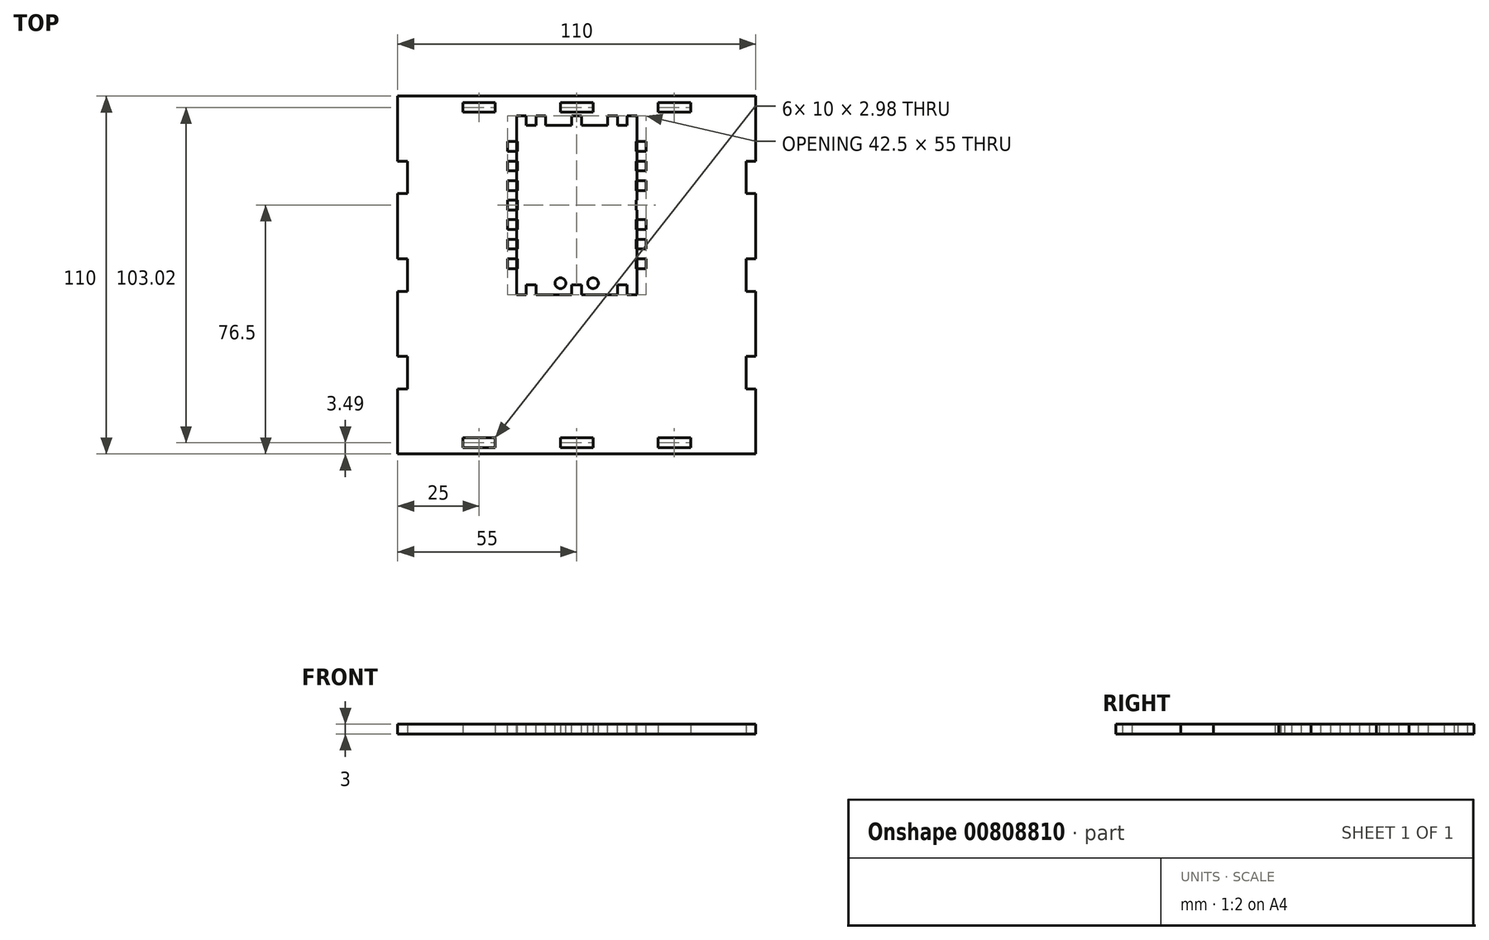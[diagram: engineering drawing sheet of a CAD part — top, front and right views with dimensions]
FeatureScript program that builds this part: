
annotation { "Feature Type Name" : "Feature", "Feature Type Description" : "" }
export const myFeature = defineFeature(function(context is Context, id is Id, definition is map)
    precondition{}
    {
        {
            var Q0;
            Q0=qCreatedBy(makeId("Top.planeOp"),FACE);
            var sketch = newSketch(context, id + "F0", { "sketchPlane" : qUnion([Q0])});
            skLineSegment(sketch, "E0.bottom", {"start": v(56, 56) * mm, "end": v(-56, 56) * mm});
            skLineSegment(sketch, "E0.top", {"start": v(56, -56) * mm, "end": v(-56, -56) * mm});
            skLineSegment(sketch, "E0.left", {"start": v(56, 56) * mm, "end": v(56, -56) * mm});
            skLineSegment(sketch, "E0.right", {"start": v(-56, 56) * mm, "end": v(-56, -56) * mm});
            skLineSegment(sketch, "E1.bottom", {"start": v(5, 50.01) * mm, "end": v(-5, 50.01) * mm});
            skLineSegment(sketch, "E1.top", {"start": v(5, 52.99) * mm, "end": v(-5, 52.99) * mm});
            skLineSegment(sketch, "E1.left", {"start": v(5, 50.01) * mm, "end": v(5, 52.99) * mm});
            skLineSegment(sketch, "E1.right", {"start": v(-5, 50) * mm, "end": v(-5, 52.99) * mm});
            skPoint(sketch, "E1.middle", {"position": v(0, 51.5) * mm});
            skLineSegment(sketch, "E2.bottom", {"start": v(-35, 50.01) * mm, "end": v(-25, 50.01) * mm});
            skLineSegment(sketch, "E2.top", {"start": v(-35, 53) * mm, "end": v(-25, 53) * mm});
            skLineSegment(sketch, "E2.left", {"start": v(-35, 50.01) * mm, "end": v(-35, 52.99) * mm});
            skLineSegment(sketch, "E2.right", {"start": v(-25, 50.01) * mm, "end": v(-25, 52.99) * mm});
            skPoint(sketch, "E2.middle", {"position": v(-30, 51.5) * mm});
            skLineSegment(sketch, "E3.bottom", {"start": v(35, 50.01) * mm, "end": v(25, 50.01) * mm});
            skLineSegment(sketch, "E3.top", {"start": v(35, 52.99) * mm, "end": v(25, 52.99) * mm});
            skLineSegment(sketch, "E3.left", {"start": v(35, 50) * mm, "end": v(35, 52.99) * mm});
            skLineSegment(sketch, "E3.right", {"start": v(25, 50) * mm, "end": v(25, 52.99) * mm});
            skPoint(sketch, "E3.middle", {"position": v(30, 51.5) * mm});
            skPoint(sketch, "E3.cornerSnap0", {"position": v(0, 50.01) * mm});
            skLineSegment(sketch, "E4.2.0", {"start": v(35, -53) * mm, "end": v(25, -53) * mm});
            skLineSegment(sketch, "E4.2.1", {"start": v(35, -50.03) * mm, "end": v(25, -50.03) * mm});
            skPoint(sketch, "E4.2.2", {"position": v(-30, -51.5) * mm});
            skLineSegment(sketch, "E4.2.3", {"start": v(-5, -53) * mm, "end": v(5, -53) * mm});
            skLineSegment(sketch, "E4.2.4", {"start": v(-35, -50.03) * mm, "end": v(-25, -50.03) * mm});
            skPoint(sketch, "E4.2.5", {"position": v(0, -50.01) * mm});
            skPoint(sketch, "E4.2.6", {"position": v(0, -51.5) * mm});
            skPoint(sketch, "E4.2.7", {"position": v(30, -51.5) * mm});
            skLineSegment(sketch, "E4.2.8", {"start": v(-5, -50.03) * mm, "end": v(5, -50.03) * mm});
            skLineSegment(sketch, "E4.2.9", {"start": v(-35, -53) * mm, "end": v(-25, -53) * mm});
            skLineSegment(sketch, "E4.2.10", {"start": v(35, -50.03) * mm, "end": v(35, -53) * mm});
            skLineSegment(sketch, "E4.2.11", {"start": v(-35, -50.03) * mm, "end": v(-35, -53) * mm});
            skLineSegment(sketch, "E4.2.12", {"start": v(-5, -50.03) * mm, "end": v(-5, -53) * mm});
            skLineSegment(sketch, "E4.2.13", {"start": v(-25, -50.03) * mm, "end": v(-25, -53) * mm});
            skLineSegment(sketch, "E4.2.14", {"start": v(5, -50.03) * mm, "end": v(5, -53) * mm});
            skLineSegment(sketch, "E4.2.15", {"start": v(25, -50.03) * mm, "end": v(25, -53) * mm});
            skLineSegment(sketch, "E5.bottom", {"start": v(-55, -55) * mm, "end": v(55, -55) * mm});
            skLineSegment(sketch, "E5.top", {"start": v(-55, 55) * mm, "end": v(55, 55) * mm});
            skLineSegment(sketch, "E5.left", {"start": v(-55, -55.01) * mm, "end": v(-55, 55) * mm});
            skLineSegment(sketch, "E5.right", {"start": v(55, -55) * mm, "end": v(55, 55) * mm});
            skLineSegment(sketch, "E6.bottom", {"start": v(-52, 4.99) * mm, "end": v(-58, 4.99) * mm});
            skLineSegment(sketch, "E6.top", {"start": v(-52, -5.01) * mm, "end": v(-58, -5.01) * mm});
            skLineSegment(sketch, "E6.left", {"start": v(-52, 4.99) * mm, "end": v(-52, -5.01) * mm});
            skLineSegment(sketch, "E6.right", {"start": v(-58, 4.99) * mm, "end": v(-58, -5.01) * mm});
            skPoint(sketch, "E6.middle", {"position": v(-55, -0.01) * mm});
            skLineSegment(sketch, "E7.bottom", {"start": v(-52, 24.99) * mm, "end": v(-58, 24.99) * mm});
            skLineSegment(sketch, "E7.top", {"start": v(-52, 34.99) * mm, "end": v(-58, 34.99) * mm});
            skLineSegment(sketch, "E7.left", {"start": v(-52, 24.99) * mm, "end": v(-52, 34.99) * mm});
            skLineSegment(sketch, "E7.right", {"start": v(-58, 24.99) * mm, "end": v(-58, 34.99) * mm});
            skPoint(sketch, "E7.middle", {"position": v(-55, 29.99) * mm});
            skLineSegment(sketch, "E8.bottom", {"start": v(-52, -25.01) * mm, "end": v(-58, -25.01) * mm});
            skLineSegment(sketch, "E8.top", {"start": v(-52, -35.01) * mm, "end": v(-58, -35.01) * mm});
            skLineSegment(sketch, "E8.left", {"start": v(-52, -25.01) * mm, "end": v(-52, -35.01) * mm});
            skLineSegment(sketch, "E8.right", {"start": v(-58, -25.01) * mm, "end": v(-58, -35.01) * mm});
            skPoint(sketch, "E8.middle", {"position": v(-55, -30.01) * mm});
            skLineSegment(sketch, "E9", {"start": v(0, 0) * mm, "end": v(0, 13.34) * mm});
            skLineSegment(sketch, "E10.MirrorCS", {"start": v(52, -35.01) * mm, "end": v(58, -35.01) * mm});
            skLineSegment(sketch, "E11.MirrorCS", {"start": v(52, -25.01) * mm, "end": v(58, -25.01) * mm});
            skLineSegment(sketch, "E12.MirrorCS", {"start": v(52, 4.99) * mm, "end": v(58, 4.99) * mm});
            skLineSegment(sketch, "E13.MirrorCS", {"start": v(52, -5.01) * mm, "end": v(58, -5.01) * mm});
            skLineSegment(sketch, "E14.MirrorCS", {"start": v(52, 35) * mm, "end": v(58, 35) * mm});
            skLineSegment(sketch, "E15.MirrorCS", {"start": v(52, 25) * mm, "end": v(58, 25) * mm});
            skLineSegment(sketch, "E16.MirrorCS", {"start": v(58, -25.01) * mm, "end": v(58, -35.01) * mm});
            skPoint(sketch, "E17.MirrorP", {"position": v(55, -30.01) * mm});
            skLineSegment(sketch, "E18.MirrorCS", {"start": v(52, 24.99) * mm, "end": v(52, 34.99) * mm});
            skPoint(sketch, "E19.MirrorP", {"position": v(55, -0.01) * mm});
            skLineSegment(sketch, "E20.MirrorCS", {"start": v(58, 4.99) * mm, "end": v(58, -5.01) * mm});
            skLineSegment(sketch, "E21.MirrorCS", {"start": v(52, -25.01) * mm, "end": v(52, -35.01) * mm});
            skPoint(sketch, "E22.MirrorP", {"position": v(55, 29.99) * mm});
            skLineSegment(sketch, "E23.MirrorCS", {"start": v(58, 24.99) * mm, "end": v(58, 34.99) * mm});
            skLineSegment(sketch, "E24.MirrorCS", {"start": v(52, 4.99) * mm, "end": v(52, -5.01) * mm});
            skSolve(sketch);
        }
        {
            var Q0;
            Q0=makeQuery(id+"F0.imprint","IMPRINT",FACE,{"disambiguationData":[TD([[makeQuery(id+"F0.imprint","IMPRINT",EDGE,{"derivedFrom":sQuery(id+"F0.wireOp",EDGE,"E1.bottom")}),1.0]])]});
            extrude(context, id + "F1", {"entities" : qUnion([Q0]), "depth" : 3 * mm, "offsetDistance" : 25 * mm});
        }
        {
            var Q0;
            Q0=makeQuery(id+"F1.opExtrude","CAP_FACE",FACE,{"disambiguationData":[OSD([sQuery(id+"F0.wireOp",EDGE,"E1.bottom"),sQuery(id+"F0.wireOp",EDGE,"E1.top"),sQuery(id+"F0.wireOp",EDGE,"E1.left"),sQuery(id+"F0.wireOp",EDGE,"E1.right"),sQuery(id+"F0.wireOp",EDGE,"E2.bottom"),sQuery(id+"F0.wireOp",EDGE,"E2.top"),sQuery(id+"F0.wireOp",EDGE,"E2.left"),sQuery(id+"F0.wireOp",EDGE,"E2.right"),sQuery(id+"F0.wireOp",EDGE,"E3.bottom"),sQuery(id+"F0.wireOp",EDGE,"E3.top"),sQuery(id+"F0.wireOp",EDGE,"E3.left"),sQuery(id+"F0.wireOp",EDGE,"E3.right"),sQuery(id+"F0.wireOp",EDGE,"E4.2.0"),sQuery(id+"F0.wireOp",EDGE,"E4.2.1"),sQuery(id+"F0.wireOp",EDGE,"E4.2.3"),sQuery(id+"F0.wireOp",EDGE,"E4.2.4"),sQuery(id+"F0.wireOp",EDGE,"E4.2.8"),sQuery(id+"F0.wireOp",EDGE,"E4.2.9"),sQuery(id+"F0.wireOp",EDGE,"E4.2.10"),sQuery(id+"F0.wireOp",EDGE,"E4.2.11"),sQuery(id+"F0.wireOp",EDGE,"E4.2.12"),sQuery(id+"F0.wireOp",EDGE,"E4.2.13"),sQuery(id+"F0.wireOp",EDGE,"E4.2.14"),sQuery(id+"F0.wireOp",EDGE,"E4.2.15"),sQuery(id+"F0.wireOp",EDGE,"0zcDC3ib-bcg3-5sZ6-BDiP-zJexwXc4272b.bottom"),sQuery(id+"F0.wireOp",EDGE,"0zcDC3ib-bcg3-5sZ6-BDiP-zJexwXc4272b.top"),sQuery(id+"F0.wireOp",EDGE,"0zcDC3ib-bcg3-5sZ6-BDiP-zJexwXc4272b.left"),sQuery(id+"F0.wireOp",EDGE,"0zcDC3ib-bcg3-5sZ6-BDiP-zJexwXc4272b.right"),sQuery(id+"F0.wireOp",EDGE,"AYckzOQu-6AoG-rlAT-OC1d-WLOSyRdi4t6B.bottom"),sQuery(id+"F0.wireOp",EDGE,"AYckzOQu-6AoG-rlAT-OC1d-WLOSyRdi4t6B.top"),sQuery(id+"F0.wireOp",EDGE,"AYckzOQu-6AoG-rlAT-OC1d-WLOSyRdi4t6B.left"),sQuery(id+"F0.wireOp",EDGE,"AYckzOQu-6AoG-rlAT-OC1d-WLOSyRdi4t6B.right"),sQuery(id+"F0.wireOp",EDGE,"v7SjSU9A-ZMWt-pp7a-Yyk7-2Wle3bSg0qv4.bottom"),sQuery(id+"F0.wireOp",EDGE,"v7SjSU9A-ZMWt-pp7a-Yyk7-2Wle3bSg0qv4.top"),sQuery(id+"F0.wireOp",EDGE,"v7SjSU9A-ZMWt-pp7a-Yyk7-2Wle3bSg0qv4.left"),sQuery(id+"F0.wireOp",EDGE,"v7SjSU9A-ZMWt-pp7a-Yyk7-2Wle3bSg0qv4.right"),sQuery(id+"F0.wireOp",EDGE,"be98ada6-46cd-47df-a602-7366731bf80c0.MirrorCS"),sQuery(id+"F0.wireOp",EDGE,"be98ada6-46cd-47df-a602-7366731bf80c1.MirrorCS"),sQuery(id+"F0.wireOp",EDGE,"be98ada6-46cd-47df-a602-7366731bf80c2.MirrorCS"),sQuery(id+"F0.wireOp",EDGE,"be98ada6-46cd-47df-a602-7366731bf80c3.MirrorCS"),sQuery(id+"F0.wireOp",EDGE,"be98ada6-46cd-47df-a602-7366731bf80c4.MirrorCS"),sQuery(id+"F0.wireOp",EDGE,"be98ada6-46cd-47df-a602-7366731bf80c5.MirrorCS"),sQuery(id+"F0.wireOp",EDGE,"be98ada6-46cd-47df-a602-7366731bf80c6.MirrorCS"),sQuery(id+"F0.wireOp",EDGE,"be98ada6-46cd-47df-a602-7366731bf80c7.MirrorCS"),sQuery(id+"F0.wireOp",EDGE,"be98ada6-46cd-47df-a602-7366731bf80c8.MirrorCS"),sQuery(id+"F0.wireOp",EDGE,"be98ada6-46cd-47df-a602-7366731bf80c10.MirrorCS"),sQuery(id+"F0.wireOp",EDGE,"be98ada6-46cd-47df-a602-7366731bf80c11.MirrorCS"),sQuery(id+"F0.wireOp",EDGE,"be98ada6-46cd-47df-a602-7366731bf80c12.MirrorCS"),sQuery(id+"F0.wireOp",EDGE,"E5.bottom"),sQuery(id+"F0.wireOp",EDGE,"E5.top"),sQuery(id+"F0.wireOp",EDGE,"E5.left"),sQuery(id+"F0.wireOp",EDGE,"E5.right")])],"isStart":false});
            var sketch = newSketch(context, id + "F2", { "sketchPlane" : qUnion([Q0])});
            skLineSegment(sketch, "E25.bottom", {"start": v(21.25, -6) * mm, "end": v(-21.25, -6) * mm});
            skLineSegment(sketch, "E25.top", {"start": v(21.25, 49) * mm, "end": v(-21.25, 49) * mm});
            skLineSegment(sketch, "E25.left", {"start": v(21.25, -6) * mm, "end": v(21.25, 49) * mm});
            skLineSegment(sketch, "E25.right", {"start": v(-21.25, -6.01) * mm, "end": v(-21.25, 49) * mm});
            skPoint(sketch, "E25.middle", {"position": v(0, 21.5) * mm});
            skLineSegment(sketch, "E26.bottom", {"start": v(-18.25, 19.99) * mm, "end": v(-24.25, 19.99) * mm});
            skLineSegment(sketch, "E26.top", {"start": v(-18.25, 22.99) * mm, "end": v(-24.25, 22.99) * mm});
            skLineSegment(sketch, "E26.left", {"start": v(-18.25, 19.99) * mm, "end": v(-18.25, 22.99) * mm});
            skLineSegment(sketch, "E26.right", {"start": v(-24.25, 19.99) * mm, "end": v(-24.25, 22.99) * mm});
            skPoint(sketch, "E26.middle", {"position": v(-21.25, 21.49) * mm});
            skLineSegment(sketch, "E27.bottom", {"start": v(24.25, 20) * mm, "end": v(18.25, 20) * mm});
            skLineSegment(sketch, "E27.top", {"start": v(24.25, 23) * mm, "end": v(18.25, 23) * mm});
            skLineSegment(sketch, "E27.left", {"start": v(24.25, 20) * mm, "end": v(24.25, 23) * mm});
            skLineSegment(sketch, "E27.right", {"start": v(18.25, 20) * mm, "end": v(18.25, 23) * mm});
            skPoint(sketch, "E27.middle", {"position": v(21.25, 21.5) * mm});
            skLineSegment(sketch, "E28.bottom", {"start": v(1.5, -9) * mm, "end": v(-1.5, -9) * mm});
            skLineSegment(sketch, "E28.top", {"start": v(1.5, -3) * mm, "end": v(-1.5, -3) * mm});
            skLineSegment(sketch, "E28.left", {"start": v(1.5, -9) * mm, "end": v(1.5, -3) * mm});
            skLineSegment(sketch, "E28.right", {"start": v(-1.5, -9) * mm, "end": v(-1.5, -3) * mm});
            skPoint(sketch, "E28.middle", {"position": v(0, -6) * mm});
            skLineSegment(sketch, "E29.bottom", {"start": v(1.5, 45.99) * mm, "end": v(-1.5, 45.99) * mm});
            skLineSegment(sketch, "E29.top", {"start": v(1.5, 52) * mm, "end": v(-1.5, 52) * mm});
            skLineSegment(sketch, "E29.left", {"start": v(1.5, 46) * mm, "end": v(1.5, 52) * mm});
            skLineSegment(sketch, "E29.right", {"start": v(-1.5, 46) * mm, "end": v(-1.5, 52) * mm});
            skPoint(sketch, "E29.middle", {"position": v(0, 49) * mm});
            skLineSegment(sketch, "E30.bottom", {"start": v(-9.7, 1.54) * mm, "end": v(9.7, 1.54) * mm});
            skLineSegment(sketch, "E30.top", {"start": v(-9.7, 41.44) * mm, "end": v(9.7, 41.44) * mm});
            skLineSegment(sketch, "E30.left", {"start": v(-9.7, 1.54) * mm, "end": v(-9.7, 41.44) * mm});
            skLineSegment(sketch, "E30.right", {"start": v(9.7, 1.54) * mm, "end": v(9.7, 41.44) * mm});
            skLineSegment(sketch, "E31.bottom", {"start": v(-18.25, 13.99) * mm, "end": v(-24.25, 13.99) * mm});
            skLineSegment(sketch, "E31.top", {"start": v(-18.25, 16.99) * mm, "end": v(-24.25, 16.99) * mm});
            skLineSegment(sketch, "E31.left", {"start": v(-18.25, 13.99) * mm, "end": v(-18.25, 16.99) * mm});
            skLineSegment(sketch, "E31.right", {"start": v(-24.25, 13.99) * mm, "end": v(-24.25, 16.99) * mm});
            skPoint(sketch, "E31.middle", {"position": v(-21.25, 15.5) * mm});
            skLineSegment(sketch, "E32.bottom", {"start": v(-18.25, 25.99) * mm, "end": v(-24.25, 25.99) * mm});
            skLineSegment(sketch, "E32.top", {"start": v(-18.25, 28.99) * mm, "end": v(-24.25, 28.99) * mm});
            skLineSegment(sketch, "E32.left", {"start": v(-18.25, 25.99) * mm, "end": v(-18.25, 28.99) * mm});
            skLineSegment(sketch, "E32.right", {"start": v(-24.25, 25.99) * mm, "end": v(-24.25, 28.99) * mm});
            skPoint(sketch, "E32.middle", {"position": v(-21.25, 27.49) * mm});
            skLineSegment(sketch, "E33.bottom", {"start": v(-18.25, 31.99) * mm, "end": v(-24.25, 31.99) * mm});
            skLineSegment(sketch, "E33.top", {"start": v(-18.25, 34.99) * mm, "end": v(-24.25, 34.99) * mm});
            skLineSegment(sketch, "E33.left", {"start": v(-18.25, 31.99) * mm, "end": v(-18.25, 34.99) * mm});
            skLineSegment(sketch, "E33.right", {"start": v(-24.25, 31.99) * mm, "end": v(-24.25, 35) * mm});
            skPoint(sketch, "E33.middle", {"position": v(-21.25, 33.49) * mm});
            skLineSegment(sketch, "E34.bottom", {"start": v(-18.25, 8) * mm, "end": v(-24.25, 8) * mm});
            skLineSegment(sketch, "E34.top", {"start": v(-18.25, 11) * mm, "end": v(-24.25, 11) * mm});
            skLineSegment(sketch, "E34.left", {"start": v(-18.25, 8) * mm, "end": v(-18.25, 11) * mm});
            skLineSegment(sketch, "E34.right", {"start": v(-24.25, 8) * mm, "end": v(-24.25, 11) * mm});
            skPoint(sketch, "E34.middle", {"position": v(-21.25, 9.5) * mm});
            skLineSegment(sketch, "E35.bottom", {"start": v(-18.25, 37.99) * mm, "end": v(-24.25, 37.99) * mm});
            skLineSegment(sketch, "E35.top", {"start": v(-18.25, 41) * mm, "end": v(-24.25, 41) * mm});
            skLineSegment(sketch, "E35.left", {"start": v(-18.25, 37.99) * mm, "end": v(-18.25, 41) * mm});
            skLineSegment(sketch, "E35.right", {"start": v(-24.25, 37.99) * mm, "end": v(-24.25, 41) * mm});
            skPoint(sketch, "E35.middle", {"position": v(-21.25, 39.49) * mm});
            skLineSegment(sketch, "E36.bottom", {"start": v(-18.25, 2) * mm, "end": v(-24.25, 1.99) * mm});
            skLineSegment(sketch, "E36.top", {"start": v(-18.25, 4.99) * mm, "end": v(-24.25, 4.99) * mm});
            skLineSegment(sketch, "E36.left", {"start": v(-18.25, 2) * mm, "end": v(-18.25, 4.99) * mm});
            skLineSegment(sketch, "E36.right", {"start": v(-24.25, 1.99) * mm, "end": v(-24.25, 4.99) * mm});
            skPoint(sketch, "E36.middle", {"position": v(-21.25, 3.5) * mm});
            skLineSegment(sketch, "E37", {"start": v(0, 21.5) * mm, "end": v(0, 24.95) * mm});
            skLineSegment(sketch, "E38.MirrorCS", {"start": v(24.25, 25.99) * mm, "end": v(24.25, 28.99) * mm});
            skLineSegment(sketch, "E39.MirrorCS", {"start": v(24.25, 8) * mm, "end": v(24.25, 11) * mm});
            skLineSegment(sketch, "E40.MirrorCS", {"start": v(18.25, 8) * mm, "end": v(18.25, 11) * mm});
            skLineSegment(sketch, "E41.MirrorCS", {"start": v(18.25, 31.99) * mm, "end": v(18.25, 34.99) * mm});
            skLineSegment(sketch, "E42.MirrorCS", {"start": v(18.25, 19.99) * mm, "end": v(18.25, 22.99) * mm});
            skLineSegment(sketch, "E43.MirrorCS", {"start": v(24.25, 19.99) * mm, "end": v(24.25, 22.99) * mm});
            skLineSegment(sketch, "E44.MirrorCS", {"start": v(18.25, 25.99) * mm, "end": v(18.25, 28.99) * mm});
            skLineSegment(sketch, "E45.MirrorCS", {"start": v(18.25, 37.99) * mm, "end": v(18.25, 41) * mm});
            skLineSegment(sketch, "E46.MirrorCS", {"start": v(24.25, 31.99) * mm, "end": v(24.25, 35) * mm});
            skLineSegment(sketch, "E47.MirrorCS", {"start": v(24.25, 37.99) * mm, "end": v(24.25, 41) * mm});
            skLineSegment(sketch, "E48.MirrorCS", {"start": v(18.25, 31.99) * mm, "end": v(24.25, 31.99) * mm});
            skLineSegment(sketch, "E49.MirrorCS", {"start": v(18.25, 17) * mm, "end": v(24.25, 17) * mm});
            skLineSegment(sketch, "E50.MirrorCS", {"start": v(18.25, 41) * mm, "end": v(24.25, 41) * mm});
            skLineSegment(sketch, "E51.MirrorCS", {"start": v(18.25, 20) * mm, "end": v(24.25, 20) * mm});
            skLineSegment(sketch, "E52.MirrorCS", {"start": v(18.25, 23) * mm, "end": v(24.25, 23) * mm});
            skLineSegment(sketch, "E53.MirrorCS", {"start": v(18.25, 37.99) * mm, "end": v(24.25, 37.99) * mm});
            skLineSegment(sketch, "E54.MirrorCS", {"start": v(18.25, 35) * mm, "end": v(24.25, 35) * mm});
            skLineSegment(sketch, "E55.MirrorCS", {"start": v(18.25, 11) * mm, "end": v(24.25, 11) * mm});
            skLineSegment(sketch, "E56.MirrorCS", {"start": v(18.25, 25.99) * mm, "end": v(24.25, 25.99) * mm});
            skLineSegment(sketch, "E57.MirrorCS", {"start": v(18.25, 2) * mm, "end": v(24.25, 2) * mm});
            skLineSegment(sketch, "E58.MirrorCS", {"start": v(18.25, 28.99) * mm, "end": v(24.25, 28.99) * mm});
            skLineSegment(sketch, "E59.MirrorCS", {"start": v(18.25, 8) * mm, "end": v(24.25, 8) * mm});
            skLineSegment(sketch, "E60.MirrorCS", {"start": v(24.25, 1.99) * mm, "end": v(24.25, 4.99) * mm});
            skLineSegment(sketch, "E61.MirrorCS", {"start": v(18.25, 14) * mm, "end": v(24.25, 14) * mm});
            skPoint(sketch, "E62.MirrorP", {"position": v(21.25, 15.5) * mm});
            skPoint(sketch, "E63.MirrorP", {"position": v(21.25, 27.49) * mm});
            skLineSegment(sketch, "E64.MirrorCS", {"start": v(18.25, 2) * mm, "end": v(18.25, 4.99) * mm});
            skPoint(sketch, "E65.MirrorP", {"position": v(21.25, 39.49) * mm});
            skLineSegment(sketch, "E66.MirrorCS", {"start": v(18.25, 13.99) * mm, "end": v(18.25, 16.99) * mm});
            skPoint(sketch, "E67.MirrorP", {"position": v(21.25, 33.49) * mm});
            skLineSegment(sketch, "E68.MirrorCS", {"start": v(18.25, 5) * mm, "end": v(24.25, 5) * mm});
            skPoint(sketch, "E69.MirrorP", {"position": v(21.25, 9.5) * mm});
            skLineSegment(sketch, "E70.MirrorCS", {"start": v(24.25, 13.99) * mm, "end": v(24.25, 16.99) * mm});
            skPoint(sketch, "E71.MirrorP", {"position": v(21.25, 3.5) * mm});
            skCircle(sketch, "E72", {"center": v(5, 45.5) * mm, "radius": 1.65 * mm});
            skCircle(sketch, "E73", {"center": v(-5, 45.5) * mm, "radius": 1.65 * mm});
            skCircle(sketch, "E74", {"center": v(-5, -2.5) * mm, "radius": 1.65 * mm});
            skCircle(sketch, "E75", {"center": v(5, -2.5) * mm, "radius": 1.65 * mm});
            skLineSegment(sketch, "E76.bottom", {"start": v(-12.5, 46) * mm, "end": v(-9.5, 46) * mm});
            skLineSegment(sketch, "E76.top", {"start": v(-12.5, 52) * mm, "end": v(-9.5, 52) * mm});
            skLineSegment(sketch, "E76.left", {"start": v(-12.5, 46) * mm, "end": v(-12.5, 52) * mm});
            skLineSegment(sketch, "E76.right", {"start": v(-9.5, 46) * mm, "end": v(-9.5, 52) * mm});
            skPoint(sketch, "E76.middle", {"position": v(-11, 49) * mm});
            skLineSegment(sketch, "E77.bottom", {"start": v(-15.5, 46) * mm, "end": v(-18.5, 46) * mm});
            skLineSegment(sketch, "E77.top", {"start": v(-15.5, 52) * mm, "end": v(-18.5, 52) * mm});
            skLineSegment(sketch, "E77.left", {"start": v(-15.5, 46) * mm, "end": v(-15.5, 52) * mm});
            skLineSegment(sketch, "E77.right", {"start": v(-18.5, 46) * mm, "end": v(-18.5, 52) * mm});
            skPoint(sketch, "E77.middle", {"position": v(-17, 49) * mm});
            skLineSegment(sketch, "E78.MirrorCS", {"start": v(9.5, 46) * mm, "end": v(9.5, 52) * mm});
            skLineSegment(sketch, "E79.MirrorCS", {"start": v(12.5, 52) * mm, "end": v(9.5, 52) * mm});
            skLineSegment(sketch, "E80.MirrorCS", {"start": v(12.5, 46) * mm, "end": v(12.5, 52) * mm});
            skLineSegment(sketch, "E81.MirrorCS", {"start": v(12.5, 46) * mm, "end": v(9.5, 46) * mm});
            skLineSegment(sketch, "E82.MirrorCS", {"start": v(15.5, 46) * mm, "end": v(18.5, 46) * mm});
            skLineSegment(sketch, "E83.MirrorCS", {"start": v(15.5, 46) * mm, "end": v(15.5, 52) * mm});
            skLineSegment(sketch, "E84.MirrorCS", {"start": v(15.5, 52) * mm, "end": v(18.5, 52) * mm});
            skLineSegment(sketch, "E85.MirrorCS", {"start": v(18.5, 46) * mm, "end": v(18.5, 52) * mm});
            skPoint(sketch, "E86.MirrorP", {"position": v(11, 49) * mm});
            skPoint(sketch, "E87.MirrorP", {"position": v(17, 49) * mm});
            skLineSegment(sketch, "E88", {"start": v(0, 21.5) * mm, "end": v(5.15, 21.5) * mm});
            skLineSegment(sketch, "E89.MirrorCS", {"start": v(-15.5, -9) * mm, "end": v(-18.5, -9) * mm});
            skLineSegment(sketch, "E90.MirrorCS", {"start": v(-12.5, -9) * mm, "end": v(-9.5, -9) * mm});
            skLineSegment(sketch, "E91.MirrorCS", {"start": v(-15.5, -3) * mm, "end": v(-18.5, -3) * mm});
            skLineSegment(sketch, "E92.MirrorCS", {"start": v(15.5, -3) * mm, "end": v(18.5, -3) * mm});
            skLineSegment(sketch, "E93.MirrorCS", {"start": v(12.5, -3) * mm, "end": v(9.5, -3) * mm});
            skLineSegment(sketch, "E94.MirrorCS", {"start": v(12.5, -9) * mm, "end": v(9.5, -9) * mm});
            skLineSegment(sketch, "E95.MirrorCS", {"start": v(15.5, -9) * mm, "end": v(18.5, -9) * mm});
            skLineSegment(sketch, "E96.MirrorCS", {"start": v(-12.5, -3) * mm, "end": v(-9.5, -3) * mm});
            skLineSegment(sketch, "E97.MirrorCS", {"start": v(-9.5, -3) * mm, "end": v(-9.5, -9) * mm});
            skLineSegment(sketch, "E98.MirrorCS", {"start": v(-18.5, -3) * mm, "end": v(-18.5, -9) * mm});
            skLineSegment(sketch, "E99.MirrorCS", {"start": v(9.5, -3) * mm, "end": v(9.5, -9) * mm});
            skLineSegment(sketch, "E100.MirrorCS", {"start": v(-15.5, -3) * mm, "end": v(-15.5, -9) * mm});
            skLineSegment(sketch, "E101.MirrorCS", {"start": v(12.5, -3) * mm, "end": v(12.5, -9) * mm});
            skLineSegment(sketch, "E102.MirrorCS", {"start": v(-12.5, -3) * mm, "end": v(-12.5, -9) * mm});
            skLineSegment(sketch, "E103.MirrorCS", {"start": v(21.25, 48.99) * mm, "end": v(21.25, -6) * mm});
            skLineSegment(sketch, "E104.MirrorCS", {"start": v(15.5, -3) * mm, "end": v(15.5, -9) * mm});
            skLineSegment(sketch, "E105.MirrorCS", {"start": v(18.5, -3) * mm, "end": v(18.5, -9) * mm});
            skLineSegment(sketch, "E106.MirrorCS", {"start": v(-1.5, -3) * mm, "end": v(-1.5, -9) * mm});
            skLineSegment(sketch, "E107.MirrorCS", {"start": v(1.5, -3) * mm, "end": v(1.5, -9) * mm});
            skLineSegment(sketch, "E108.MirrorCS", {"start": v(21.25, 49) * mm, "end": v(21.25, -6) * mm});
            skPoint(sketch, "E109.MirrorP", {"position": v(11, -6) * mm});
            skPoint(sketch, "E110.MirrorP", {"position": v(-17, -6) * mm});
            skPoint(sketch, "E111.MirrorP", {"position": v(-11, -6) * mm});
            skPoint(sketch, "E112.MirrorP", {"position": v(17, -6) * mm});
            skLineSegment(sketch, "E113.MirrorCS", {"start": v(-21.25, 49) * mm, "end": v(-21.25, -6) * mm});
            skLineSegment(sketch, "E114.bottom", {"start": v(-18.5, 46) * mm, "end": v(18.5, 46) * mm});
            skLineSegment(sketch, "E114.top", {"start": v(-18.5, -3) * mm, "end": v(18.5, -3) * mm});
            skLineSegment(sketch, "E114.left", {"start": v(-18.5, 46) * mm, "end": v(-18.5, -3) * mm});
            skLineSegment(sketch, "E114.right", {"start": v(18.5, 46) * mm, "end": v(18.5, -3) * mm});
            skSolve(sketch);
        }
        {
            var Q0;
            {var subQ0=sQuery(id+"F2.wireOp",EDGE,"E114.left");var subQ1=sQuery(id+"F2.wireOp",EDGE,"E35.bottom");var subQ2=makeQuery(id+"F2.imprint","INTERSECT",VERTEX,{"derivedFrom":[subQ1,subQ0]});Q0=makeQuery(id+"F2.imprint","IMPRINT",FACE,{"disambiguationData":[TD([[makeQuery(id+"F2.imprint","IMPRINT",EDGE,{"disambiguationData":[TD([[subQ2,-1.0]])],"derivedFrom":subQ1}),-1.0]])]});}
            var Q1;
            {var subQ0=sQuery(id+"F2.wireOp",EDGE,"E114.left");var subQ1=sQuery(id+"F2.wireOp",EDGE,"E33.bottom");var subQ2=makeQuery(id+"F2.imprint","INTERSECT",VERTEX,{"derivedFrom":[subQ1,subQ0]});Q1=makeQuery(id+"F2.imprint","IMPRINT",FACE,{"disambiguationData":[TD([[makeQuery(id+"F2.imprint","IMPRINT",EDGE,{"disambiguationData":[TD([[subQ2,-1.0]])],"derivedFrom":subQ1}),-1.0]])]});}
            var Q2;
            {var subQ0=sQuery(id+"F2.wireOp",EDGE,"E114.left");var subQ1=sQuery(id+"F2.wireOp",EDGE,"E32.bottom");var subQ2=makeQuery(id+"F2.imprint","INTERSECT",VERTEX,{"derivedFrom":[subQ1,subQ0]});Q2=makeQuery(id+"F2.imprint","IMPRINT",FACE,{"disambiguationData":[TD([[makeQuery(id+"F2.imprint","IMPRINT",EDGE,{"disambiguationData":[TD([[subQ2,-1.0]])],"derivedFrom":subQ1}),-1.0]])]});}
            var Q3;
            {var subQ0=sQuery(id+"F2.wireOp",EDGE,"E114.left");var subQ1=sQuery(id+"F2.wireOp",EDGE,"E26.bottom");var subQ2=makeQuery(id+"F2.imprint","INTERSECT",VERTEX,{"derivedFrom":[subQ1,subQ0]});Q3=makeQuery(id+"F2.imprint","IMPRINT",FACE,{"disambiguationData":[TD([[makeQuery(id+"F2.imprint","IMPRINT",EDGE,{"disambiguationData":[TD([[subQ2,-1.0]])],"derivedFrom":subQ1}),-1.0]])]});}
            var Q4;
            {var subQ0=sQuery(id+"F2.wireOp",EDGE,"E114.left");var subQ1=sQuery(id+"F2.wireOp",EDGE,"E31.bottom");var subQ2=makeQuery(id+"F2.imprint","INTERSECT",VERTEX,{"derivedFrom":[subQ1,subQ0]});Q4=makeQuery(id+"F2.imprint","IMPRINT",FACE,{"disambiguationData":[TD([[makeQuery(id+"F2.imprint","IMPRINT",EDGE,{"disambiguationData":[TD([[subQ2,-1.0]])],"derivedFrom":subQ1}),-1.0]])]});}
            var Q5;
            {var subQ0=sQuery(id+"F2.wireOp",EDGE,"E114.left");var subQ1=sQuery(id+"F2.wireOp",EDGE,"E34.bottom");var subQ2=makeQuery(id+"F2.imprint","INTERSECT",VERTEX,{"derivedFrom":[subQ1,subQ0]});Q5=makeQuery(id+"F2.imprint","IMPRINT",FACE,{"disambiguationData":[TD([[makeQuery(id+"F2.imprint","IMPRINT",EDGE,{"disambiguationData":[TD([[subQ2,-1.0]])],"derivedFrom":subQ1}),-1.0]])]});}
            var Q6;
            {var subQ0=sQuery(id+"F2.wireOp",EDGE,"E114.left");var subQ1=sQuery(id+"F2.wireOp",EDGE,"E36.bottom");var subQ2=makeQuery(id+"F2.imprint","INTERSECT",VERTEX,{"derivedFrom":[subQ1,subQ0]});Q6=makeQuery(id+"F2.imprint","IMPRINT",FACE,{"disambiguationData":[TD([[makeQuery(id+"F2.imprint","IMPRINT",EDGE,{"disambiguationData":[TD([[subQ2,-1.0]])],"derivedFrom":subQ1}),-1.0]])]});}
            var Q7;
            {var subQ0=sQuery(id+"F2.wireOp",EDGE,"E114.top");var subQ5=sQuery(id+"F2.wireOp",EDGE,"E100.MirrorCS");var subQ6=makeQuery(id+"F2.imprint","INTERSECT",VERTEX,{"derivedFrom":[subQ5,subQ0]});Q7=makeQuery(id+"F2.imprint","IMPRINT",FACE,{"disambiguationData":[TD([[makeQuery(id+"F2.imprint","IMPRINT",EDGE,{"disambiguationData":[TD([[subQ6,-1.0]])],"derivedFrom":subQ5}),-1.0]])]});}
            var Q8;
            {var subQ0=sQuery(id+"F2.wireOp",EDGE,"E114.top");var subQ1=sQuery(id+"F2.wireOp",EDGE,"E97.MirrorCS");var subQ2=makeQuery(id+"F2.imprint","INTERSECT",VERTEX,{"derivedFrom":[subQ1,subQ0]});Q8=makeQuery(id+"F2.imprint","IMPRINT",FACE,{"disambiguationData":[TD([[makeQuery(id+"F2.imprint","IMPRINT",EDGE,{"disambiguationData":[TD([[subQ2,-1.0]])],"derivedFrom":subQ1}),-1.0]])]});}
            var Q9;
            {var subQ0=sQuery(id+"F2.wireOp",EDGE,"E114.top");var subQ1=sQuery(id+"F2.wireOp",EDGE,"E106.MirrorCS");var subQ2=makeQuery(id+"F2.imprint","INTERSECT",VERTEX,{"derivedFrom":[subQ1,subQ0]});Q9=makeQuery(id+"F2.imprint","IMPRINT",FACE,{"disambiguationData":[TD([[makeQuery(id+"F2.imprint","IMPRINT",EDGE,{"disambiguationData":[TD([[subQ2,-1.0]])],"derivedFrom":subQ1}),1.0]])]});}
            var Q10;
            {var subQ0=sQuery(id+"F2.wireOp",EDGE,"E114.top");var subQ1=sQuery(id+"F2.wireOp",EDGE,"E99.MirrorCS");var subQ2=makeQuery(id+"F2.imprint","INTERSECT",VERTEX,{"derivedFrom":[subQ1,subQ0]});Q10=makeQuery(id+"F2.imprint","IMPRINT",FACE,{"disambiguationData":[TD([[makeQuery(id+"F2.imprint","IMPRINT",EDGE,{"disambiguationData":[TD([[subQ2,-1.0]])],"derivedFrom":subQ1}),1.0]])]});}
            var Q11;
            {var subQ0=sQuery(id+"F2.wireOp",EDGE,"E114.top");var subQ1=sQuery(id+"F2.wireOp",EDGE,"E104.MirrorCS");var subQ2=makeQuery(id+"F2.imprint","INTERSECT",VERTEX,{"derivedFrom":[subQ1,subQ0]});Q11=makeQuery(id+"F2.imprint","IMPRINT",FACE,{"disambiguationData":[TD([[makeQuery(id+"F2.imprint","IMPRINT",EDGE,{"disambiguationData":[TD([[subQ2,-1.0]])],"derivedFrom":subQ1}),1.0]])]});}
            var Q12;
            {var subQ45=sQuery(id+"F2.wireOp",EDGE,"E26.left");Q12=makeQuery(id+"F2.imprint","IMPRINT",FACE,{"disambiguationData":[TD([[makeQuery(id+"F2.imprint","IMPRINT",EDGE,{"derivedFrom":subQ45}),-1.0]])]});}
            var Q13;
            Q13=makeQuery(id+"F2.imprint","IMPRINT",FACE,{"disambiguationData":[TD([[makeQuery(id+"F2.imprint","IMPRINT",EDGE,{"derivedFrom":sQuery(id+"F2.wireOp",EDGE,"E30.bottom")}),1.0]])]});
            var Q14;
            {var subQ0=sQuery(id+"F2.wireOp",EDGE,"E114.right");var subQ1=sQuery(id+"F2.wireOp",EDGE,"E57.MirrorCS");var subQ2=makeQuery(id+"F2.imprint","INTERSECT",VERTEX,{"derivedFrom":[subQ1,subQ0]});Q14=makeQuery(id+"F2.imprint","IMPRINT",FACE,{"disambiguationData":[TD([[makeQuery(id+"F2.imprint","IMPRINT",EDGE,{"disambiguationData":[TD([[subQ2,-1.0]])],"derivedFrom":subQ1}),1.0]])]});}
            var Q15;
            {var subQ0=sQuery(id+"F2.wireOp",EDGE,"E114.right");var subQ1=sQuery(id+"F2.wireOp",EDGE,"E55.MirrorCS");var subQ2=makeQuery(id+"F2.imprint","INTERSECT",VERTEX,{"derivedFrom":[subQ1,subQ0]});Q15=makeQuery(id+"F2.imprint","IMPRINT",FACE,{"disambiguationData":[TD([[makeQuery(id+"F2.imprint","IMPRINT",EDGE,{"disambiguationData":[TD([[subQ2,-1.0]])],"derivedFrom":subQ1}),-1.0]])]});}
            var Q16;
            {var subQ0=sQuery(id+"F2.wireOp",EDGE,"E114.right");var subQ1=sQuery(id+"F2.wireOp",EDGE,"E49.MirrorCS");var subQ2=makeQuery(id+"F2.imprint","INTERSECT",VERTEX,{"derivedFrom":[subQ1,subQ0]});Q16=makeQuery(id+"F2.imprint","IMPRINT",FACE,{"disambiguationData":[TD([[makeQuery(id+"F2.imprint","IMPRINT",EDGE,{"disambiguationData":[TD([[subQ2,-1.0]])],"derivedFrom":subQ1}),-1.0]])]});}
            var Q17;
            {var subQ0=sQuery(id+"F2.wireOp",EDGE,"E114.right");var subQ1=sQuery(id+"F2.wireOp",EDGE,"E51.MirrorCS");var subQ2=makeQuery(id+"F2.imprint","INTERSECT",VERTEX,{"derivedFrom":[subQ1,subQ0]});Q17=makeQuery(id+"F2.imprint","IMPRINT",FACE,{"disambiguationData":[TD([[makeQuery(id+"F2.imprint","IMPRINT",EDGE,{"disambiguationData":[TD([[subQ2,-1.0]])],"derivedFrom":subQ1}),1.0]])]});}
            var Q18;
            {var subQ0=sQuery(id+"F2.wireOp",EDGE,"E114.right");var subQ1=sQuery(id+"F2.wireOp",EDGE,"E56.MirrorCS");var subQ2=makeQuery(id+"F2.imprint","INTERSECT",VERTEX,{"derivedFrom":[subQ1,subQ0]});Q18=makeQuery(id+"F2.imprint","IMPRINT",FACE,{"disambiguationData":[TD([[makeQuery(id+"F2.imprint","IMPRINT",EDGE,{"disambiguationData":[TD([[subQ2,-1.0]])],"derivedFrom":subQ1}),1.0]])]});}
            var Q19;
            {var subQ0=sQuery(id+"F2.wireOp",EDGE,"E114.right");var subQ1=sQuery(id+"F2.wireOp",EDGE,"E48.MirrorCS");var subQ2=makeQuery(id+"F2.imprint","INTERSECT",VERTEX,{"derivedFrom":[subQ1,subQ0]});Q19=makeQuery(id+"F2.imprint","IMPRINT",FACE,{"disambiguationData":[TD([[makeQuery(id+"F2.imprint","IMPRINT",EDGE,{"disambiguationData":[TD([[subQ2,-1.0]])],"derivedFrom":subQ1}),1.0]])]});}
            var Q20;
            {var subQ0=sQuery(id+"F2.wireOp",EDGE,"E114.right");var subQ1=sQuery(id+"F2.wireOp",EDGE,"E50.MirrorCS");var subQ2=makeQuery(id+"F2.imprint","INTERSECT",VERTEX,{"derivedFrom":[subQ1,subQ0]});Q20=makeQuery(id+"F2.imprint","IMPRINT",FACE,{"disambiguationData":[TD([[makeQuery(id+"F2.imprint","IMPRINT",EDGE,{"disambiguationData":[TD([[subQ2,-1.0]])],"derivedFrom":subQ1}),-1.0]])]});}
            var Q21;
            {var subQ0=sQuery(id+"F2.wireOp",EDGE,"E85.MirrorCS");var subQ1=sQuery(id+"F2.wireOp",EDGE,"E25.top");var subQ2=makeQuery(id+"F2.imprint","INTERSECT",VERTEX,{"derivedFrom":[subQ1,subQ0]});Q21=makeQuery(id+"F2.imprint","IMPRINT",FACE,{"disambiguationData":[TD([[makeQuery(id+"F2.imprint","IMPRINT",EDGE,{"disambiguationData":[TD([[subQ2,-1.0]])],"derivedFrom":subQ1}),1.0]])]});}
            var Q22;
            {var subQ0=sQuery(id+"F2.wireOp",EDGE,"E80.MirrorCS");var subQ1=sQuery(id+"F2.wireOp",EDGE,"E25.top");var subQ2=makeQuery(id+"F2.imprint","INTERSECT",VERTEX,{"derivedFrom":[subQ1,subQ0]});Q22=makeQuery(id+"F2.imprint","IMPRINT",FACE,{"disambiguationData":[TD([[makeQuery(id+"F2.imprint","IMPRINT",EDGE,{"disambiguationData":[TD([[subQ2,-1.0]])],"derivedFrom":subQ1}),1.0]])]});}
            var Q23;
            {var subQ0=sQuery(id+"F2.wireOp",EDGE,"E29.left");var subQ1=sQuery(id+"F2.wireOp",EDGE,"E25.top");var subQ2=makeQuery(id+"F2.imprint","INTERSECT",VERTEX,{"derivedFrom":[subQ1,subQ0]});Q23=makeQuery(id+"F2.imprint","IMPRINT",FACE,{"disambiguationData":[TD([[makeQuery(id+"F2.imprint","IMPRINT",EDGE,{"disambiguationData":[TD([[subQ2,-1.0]])],"derivedFrom":subQ1}),1.0]])]});}
            var Q24;
            {var subQ0=sQuery(id+"F2.wireOp",EDGE,"E76.right");var subQ1=sQuery(id+"F2.wireOp",EDGE,"E25.top");var subQ2=makeQuery(id+"F2.imprint","INTERSECT",VERTEX,{"derivedFrom":[subQ1,subQ0]});Q24=makeQuery(id+"F2.imprint","IMPRINT",FACE,{"disambiguationData":[TD([[makeQuery(id+"F2.imprint","IMPRINT",EDGE,{"disambiguationData":[TD([[subQ2,-1.0]])],"derivedFrom":subQ1}),1.0]])]});}
            var Q25;
            {var subQ0=sQuery(id+"F2.wireOp",EDGE,"E77.left");var subQ1=sQuery(id+"F2.wireOp",EDGE,"E25.top");var subQ2=makeQuery(id+"F2.imprint","INTERSECT",VERTEX,{"derivedFrom":[subQ1,subQ0]});Q25=makeQuery(id+"F2.imprint","IMPRINT",FACE,{"disambiguationData":[TD([[makeQuery(id+"F2.imprint","IMPRINT",EDGE,{"disambiguationData":[TD([[subQ2,-1.0]])],"derivedFrom":subQ1}),1.0]])]});}
            var Q26;
            {var subQ0=sQuery(id+"F2.wireOp",EDGE,"E114.bottom");var subQ1=sQuery(id+"F2.wireOp",EDGE,"E73");var subQ2=makeQuery(id+"F2.imprint","INTERSECT",VERTEX,{"disambiguationData":[OD(0.0)],"derivedFrom":[subQ1,subQ0]});Q26=makeQuery(id+"F2.imprint","IMPRINT",FACE,{"disambiguationData":[TD([[makeQuery(id+"F2.imprint","IMPRINT",EDGE,{"disambiguationData":[TD([[subQ2,-1.0]])],"derivedFrom":subQ1}),1.0]])]});}
            var Q27;
            {var subQ0=sQuery(id+"F2.wireOp",EDGE,"E114.bottom");var subQ1=sQuery(id+"F2.wireOp",EDGE,"E72");var subQ2=makeQuery(id+"F2.imprint","INTERSECT",VERTEX,{"disambiguationData":[OD(0.0)],"derivedFrom":[subQ1,subQ0]});Q27=makeQuery(id+"F2.imprint","IMPRINT",FACE,{"disambiguationData":[TD([[makeQuery(id+"F2.imprint","IMPRINT",EDGE,{"disambiguationData":[TD([[subQ2,-1.0]])],"derivedFrom":subQ1}),1.0]])]});}
            var Q28;
            {var subQ0=sQuery(id+"F2.wireOp",EDGE,"E114.top");var subQ1=sQuery(id+"F2.wireOp",EDGE,"E74");var subQ2=makeQuery(id+"F2.imprint","INTERSECT",VERTEX,{"disambiguationData":[OD(0.0)],"derivedFrom":[subQ1,subQ0]});Q28=makeQuery(id+"F2.imprint","IMPRINT",FACE,{"disambiguationData":[TD([[makeQuery(id+"F2.imprint","IMPRINT",EDGE,{"disambiguationData":[TD([[subQ2,-1.0]])],"derivedFrom":subQ1}),-1.0]])]});}
            var Q29;
            {var subQ0=sQuery(id+"F2.wireOp",EDGE,"E114.top");var subQ1=sQuery(id+"F2.wireOp",EDGE,"E75");var subQ2=makeQuery(id+"F2.imprint","INTERSECT",VERTEX,{"disambiguationData":[OD(0.0)],"derivedFrom":[subQ1,subQ0]});Q29=makeQuery(id+"F2.imprint","IMPRINT",FACE,{"disambiguationData":[TD([[makeQuery(id+"F2.imprint","IMPRINT",EDGE,{"disambiguationData":[TD([[subQ2,-1.0]])],"derivedFrom":subQ1}),-1.0]])]});}
            extrude(context, id + "F3", {"entities" : qUnion([Q0, Q1, Q2, Q3, Q4, Q5, Q6, Q7, Q8, Q9, Q10, Q11, Q12, Q13, Q14, Q15, Q16, Q17, Q18, Q19, Q20, Q21, Q22, Q23, Q24, Q25, Q26, Q27, Q28, Q29]), "operationType" : NewBodyOperationType.REMOVE, "oppositeDirection" : true, "depth" : 25 * mm, "offsetDistance" : 25 * mm});
        }
    });
